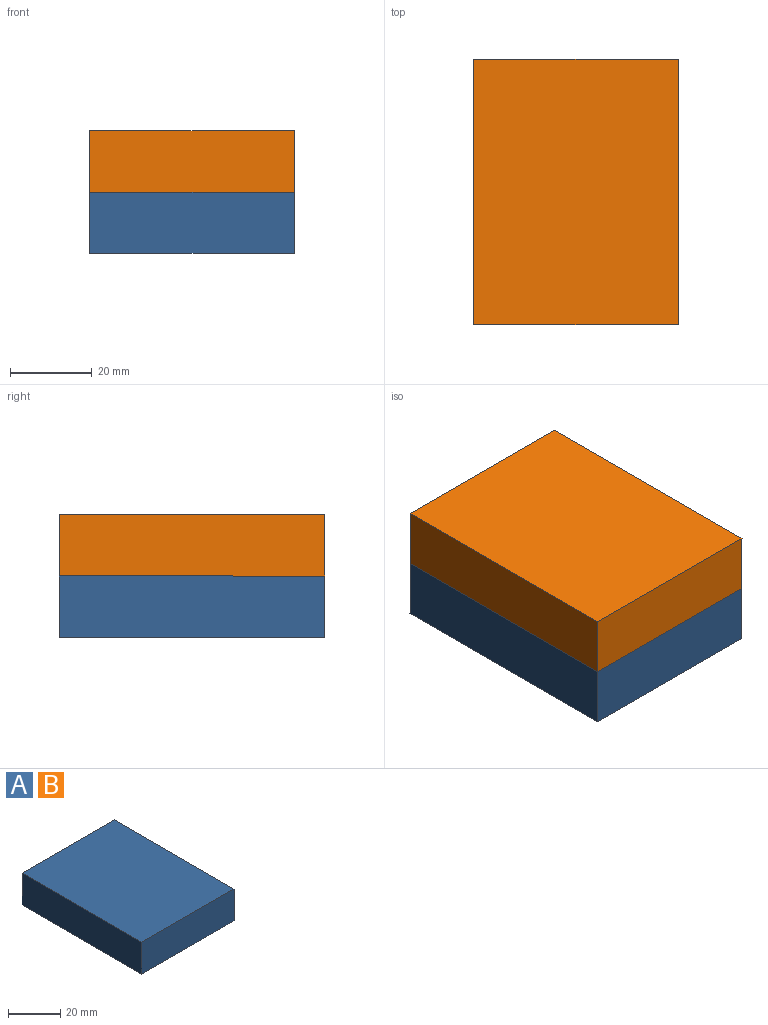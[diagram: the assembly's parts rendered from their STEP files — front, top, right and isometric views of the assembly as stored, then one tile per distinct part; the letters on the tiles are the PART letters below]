
ASSEMBLY  parts=2 mates=1
PART A: 10 faces, bbox 50x65x15 mm
  f0: plane 65x15mm, normal (1,0,0), area 912.5mm2, adj f1,f2,f4,f5,f6,f7,f9
  f1: plane 50x15mm, normal (0,-1,0), area 750mm2, adj f0,f3,f4,f5
  f2: plane 50x15mm, normal (0,1,0), area 750mm2, adj f0,f3,f4,f5
  f3: plane 65x15mm, normal (-1,0,0), area 975mm2, adj f1,f2,f4,f5
  f4: plane 65x50mm, normal (0,0,1), area 3250mm2, adj f0,f1,f2,f3
  f5: plane 65x50mm, normal (0,0,-1), area 2625mm2, adj f0,f1,f2,f3,f6,f7,f8
  f6: plane 25x2.5mm, normal (0,-1,0), area 62.5mm2, adj f0,f5,f8,f9
  f7: plane 25x2.5mm, normal (0,1,0), area 62.5mm2, adj f0,f5,f8,f9
  f8: plane 25x2.5mm, normal (1,0,0), area 62.5mm2, adj f5,f6,f7,f9
  f9: plane 25x25mm, normal (0,0,-1), area 625mm2, adj f0,f6,f7,f8
PART B: same geometry as A
PLACE A rot(axis=(-1,0,0),180deg) t=(-28.8,0.35,9.37)mm
PLACE B rot(axis=(0.93,0.37,0),0deg) t=(-28.8,0.35,9.37)mm
MATE fastened A.f5 <-> B.f5  axis (0,0,1) through (-31.77,0.35,9.37)mm
